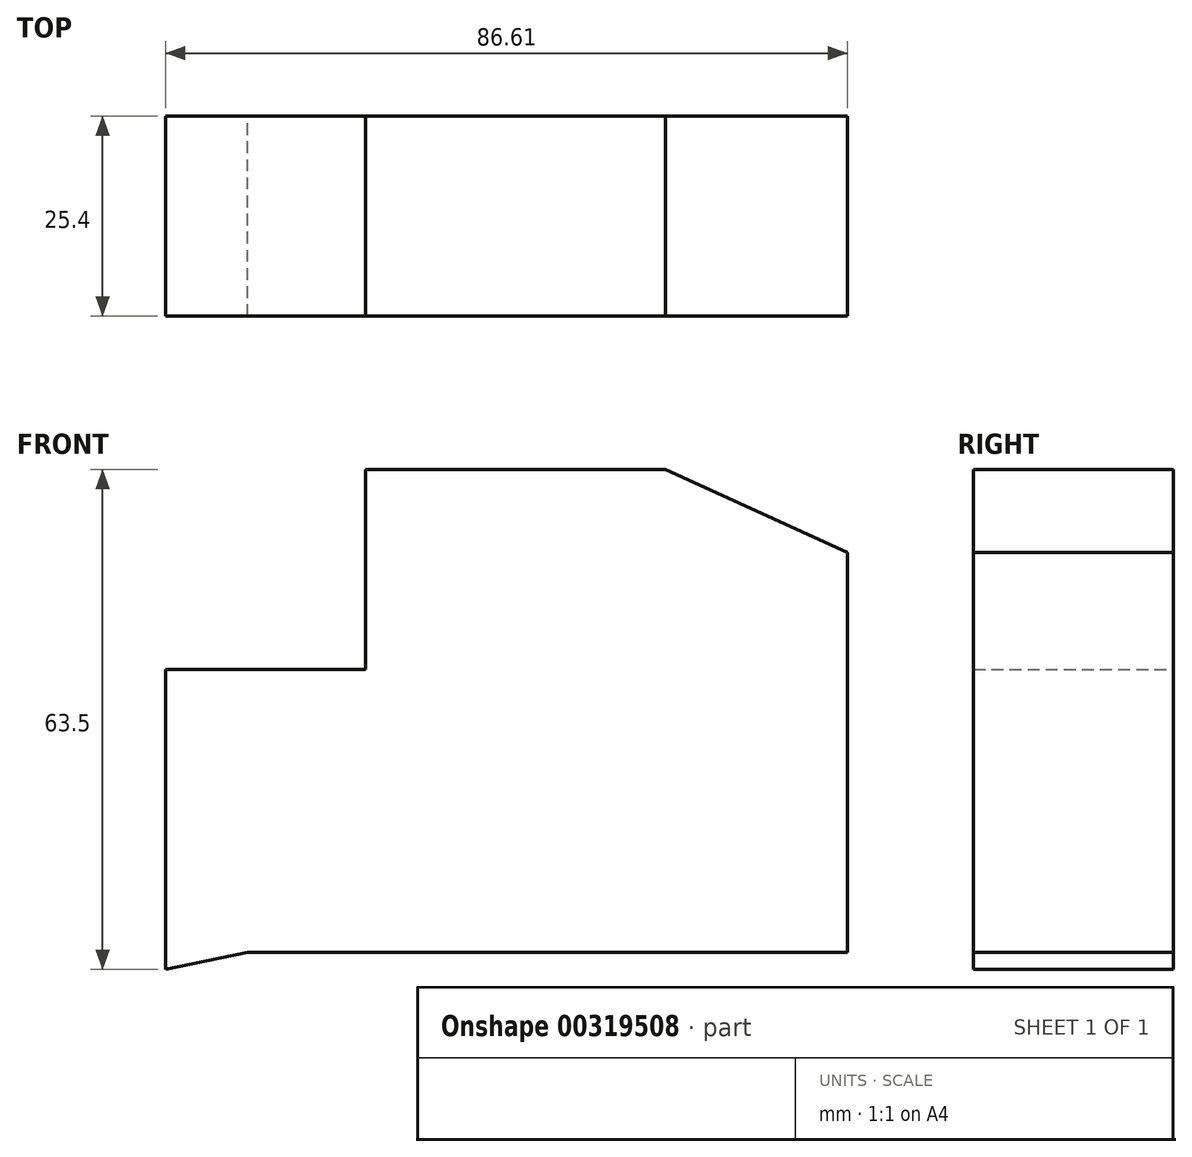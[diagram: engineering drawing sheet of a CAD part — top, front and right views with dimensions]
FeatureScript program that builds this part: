
annotation { "Feature Type Name" : "Feature", "Feature Type Description" : "" }
export const myFeature = defineFeature(function(context is Context, id is Id, definition is map)
    precondition{}
    {
        {
            var Q0;
            Q0=qCreatedBy(makeId("Front.planeOp"),FACE);
            var sketch = newSketch(context, id + "F0", { "sketchPlane" : qUnion([Q0])});
            skLineSegment(sketch, "E0", {"start": v(-42.52, -43.2) * mm, "end": v(33.68, -43.2) * mm});
            skLineSegment(sketch, "E1", {"start": v(33.68, -43.2) * mm, "end": v(33.68, 7.6) * mm});
            skLineSegment(sketch, "E2", {"start": v(33.68, 7.6) * mm, "end": v(10.57, 18.16) * mm});
            skLineSegment(sketch, "E3", {"start": v(10.57, 18.16) * mm, "end": v(-27.53, 18.16) * mm});
            skLineSegment(sketch, "E4", {"start": v(-27.53, 18.16) * mm, "end": v(-27.53, -7.24) * mm});
            skLineSegment(sketch, "E5", {"start": v(-27.53, -7.24) * mm, "end": v(-52.93, -7.24) * mm});
            skLineSegment(sketch, "E6", {"start": v(-52.93, -7.24) * mm, "end": v(-52.93, -45.34) * mm});
            skLineSegment(sketch, "E7", {"start": v(-42.52, -43.2) * mm, "end": v(-52.93, -45.34) * mm});
            skSolve(sketch);
        }
        {
            var Q0;
            Q0=makeQuery(id+"F0.imprint","IMPRINT",FACE,{"disambiguationData":[TD([[makeQuery(id+"F0.imprint","IMPRINT",EDGE,{"derivedFrom":sQuery(id+"F0.wireOp",EDGE,"E0")}),1.0]])]});
            extrude(context, id + "F1", {"entities" : qUnion([Q0]), "depth" : 25.4 * mm});
        }
    });
